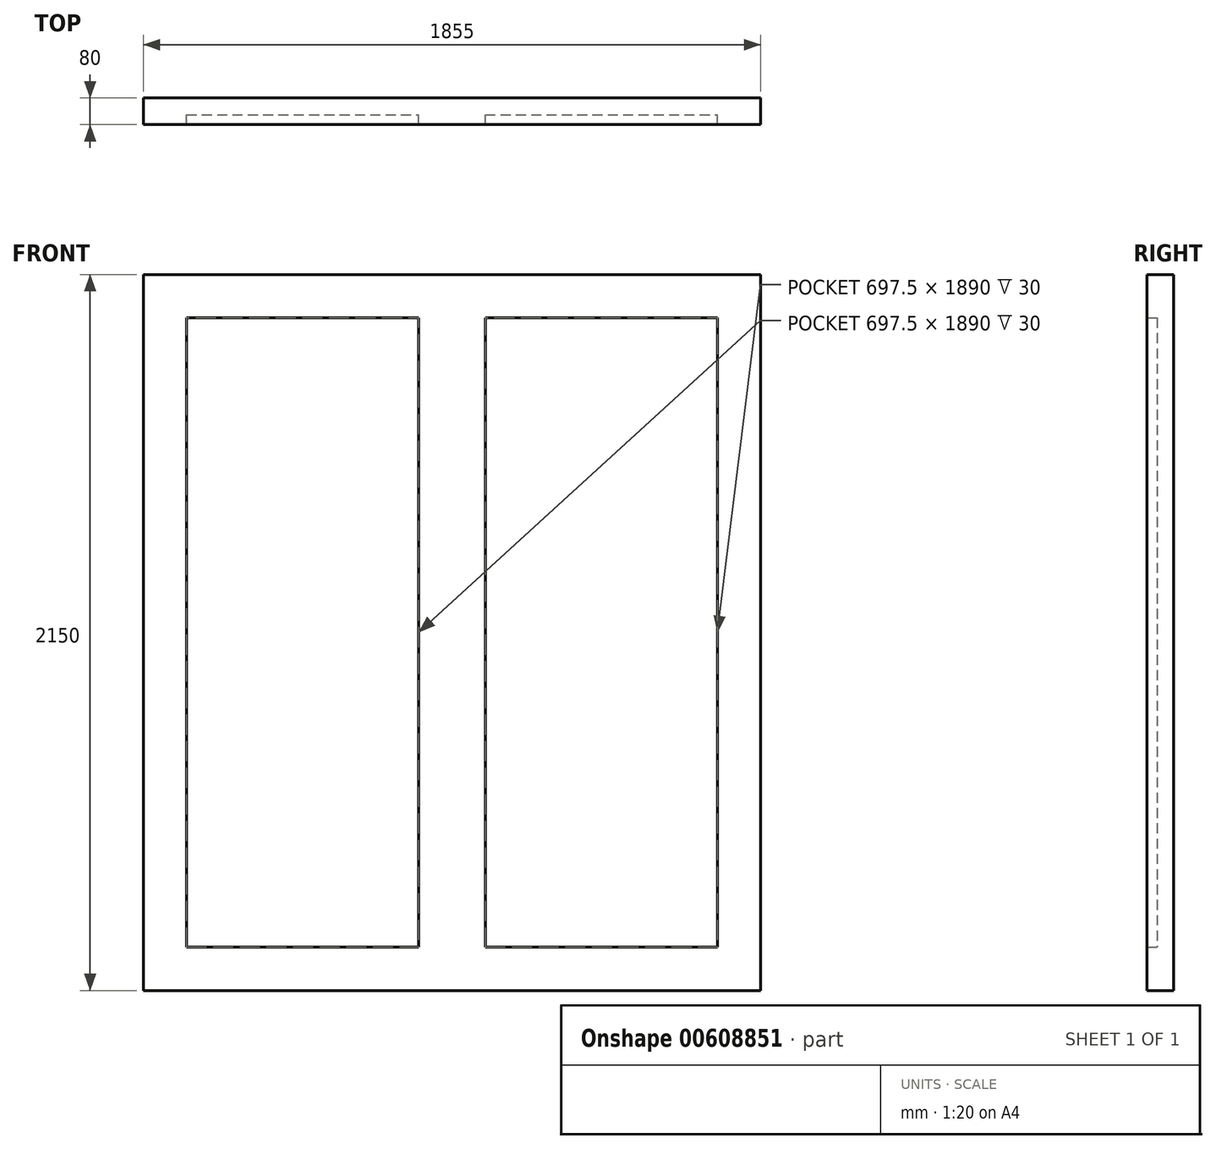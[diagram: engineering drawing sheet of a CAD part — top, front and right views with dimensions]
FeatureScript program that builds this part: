
annotation { "Feature Type Name" : "Feature", "Feature Type Description" : "" }
export const myFeature = defineFeature(function(context is Context, id is Id, definition is map)
    precondition{}
    {
        {
            var Q0;
            Q0=qCreatedBy(makeId("Front.planeOp"),FACE);
            var sketch = newSketch(context, id + "F0", { "sketchPlane" : qUnion([Q0])});
            skLineSegment(sketch, "E0.bottom", {"start": v(0, 0) * mm, "end": v(1855, 0) * mm});
            skLineSegment(sketch, "E0.top", {"start": v(0, 2150) * mm, "end": v(1855, 2150) * mm});
            skLineSegment(sketch, "E0.left", {"start": v(0, 0) * mm, "end": v(0, 2150) * mm});
            skLineSegment(sketch, "E0.right", {"start": v(1855, 0) * mm, "end": v(1855, 2150) * mm});
            skSolve(sketch);
        }
        {
            var Q0;
            Q0 = qSketchRegion(id + "F0", true);
            extrude(context, id + "F1", {"entities" : qUnion([Q0]), "depth" : 50 * mm, "offsetDistance" : 25 * mm});
        }
        {
            var Q0;
            Q0=makeQuery(id+"F1.opExtrude","CAP_FACE",FACE,{"disambiguationData":[OSD([sQuery(id+"F0.wireOp",EDGE,"E0.bottom"),sQuery(id+"F0.wireOp",EDGE,"E0.top"),sQuery(id+"F0.wireOp",EDGE,"E0.left"),sQuery(id+"F0.wireOp",EDGE,"E0.right")])],"isStart":false});
            var sketch = newSketch(context, id + "F2", { "sketchPlane" : qUnion([Q0])});
            skLineSegment(sketch, "E1", {"start": v(927.5, 2150) * mm, "end": v(927.5, 0) * mm, "construction": true});
            skLineSegment(sketch, "E2.bottom", {"start": v(130, 2020) * mm, "end": v(827.5, 2020) * mm});
            skLineSegment(sketch, "E2.top", {"start": v(130, 130) * mm, "end": v(827.5, 130) * mm});
            skLineSegment(sketch, "E2.left", {"start": v(130, 2020) * mm, "end": v(130, 130) * mm});
            skLineSegment(sketch, "E2.right", {"start": v(827.5, 2020) * mm, "end": v(827.5, 130) * mm});
            skLineSegment(sketch, "E3.bottom", {"start": v(1027.5, 2020) * mm, "end": v(1725, 2020) * mm});
            skLineSegment(sketch, "E3.top", {"start": v(1027.5, 130) * mm, "end": v(1725, 130) * mm});
            skLineSegment(sketch, "E3.left", {"start": v(1027.5, 2020) * mm, "end": v(1027.5, 130) * mm});
            skLineSegment(sketch, "E3.right", {"start": v(1725, 2020) * mm, "end": v(1725, 130) * mm});
            skLineSegment(sketch, "E4.0", {"start": v(0, 0) * mm, "end": v(0, 2150) * mm});
            skLineSegment(sketch, "E5.0", {"start": v(1855, 0) * mm, "end": v(1855, 2150) * mm});
            skLineSegment(sketch, "E6.0", {"start": v(0, 0) * mm, "end": v(1855, 0) * mm});
            skLineSegment(sketch, "E7.0", {"start": v(0, 2150) * mm, "end": v(1855, 2150) * mm});
            skSolve(sketch);
        }
        {
            var Q0;
            Q0 = qSketchRegion(id + "F2", true);
            extrude(context, id + "F3", {"entities" : qUnion([Q0]), "operationType" : NewBodyOperationType.ADD, "depth" : 30 * mm, "offsetDistance" : 25 * mm});
        }
    });
